# Revit family: Flashing_Preformed_Hyload_EndDam
name_source: partatom
category: Generic Models
revit_build: Autodesk Revit 2014 (Build: 20130308_1515(x64)
units: mm (PartAtom-declared; Revit-internal decimal feet)

## types (5) — shared parameters
Assembly Code = B3010400
Construction Details = http://www.arcat.com
Flashing Material = Hyload Flashing Membrane - Grey
Keynote = 07 65 00
Manufacturer = Hyload
Manufacturer Fax = 330-769-4153
Manufacturer Website = http://www.hyload.com
Product Data = http://www.arcat.com
Product Properties = http://www.hyload.com
Revision = R1_12-2015
Sales Information = http://www.hyload.com
Specification = http://www.arcat.com
Thickness = 0' - 0 1/16"
URL = http://www.hyload.com
Unit Depth = 0' - 4"
Unit Height = 0' - 3"

## per-type parameters (varying)
| type | Description | Model | Unit Width |
| 4 inch | Preformed Hyload Masonry Flashing - 4 in End Dam | 4 in End Dam | 0' - 4" |
| 6 inch | Preformed Hyload Masonry Flashing - 6 in End Dam | 6 in End Dam | 0' - 6" |
| 8 inch | Preformed Hyload Masonry Flashing - 8 in End Dam | 8 in End Dam | 0' - 8" |
| 10 inch | Preformed Hyload Masonry Flashing - 10 in End Dam | 10 in End Dam | 0' - 10" |
| 12 inch | Preformed Hyload Masonry Flashing - 12 in End Dam | 12 in End Dam | 1' - 0" |

## geometry (parser evidence)
native form markers: Blend x10, Sweep x3
no freeform markers — native parametric forms only
